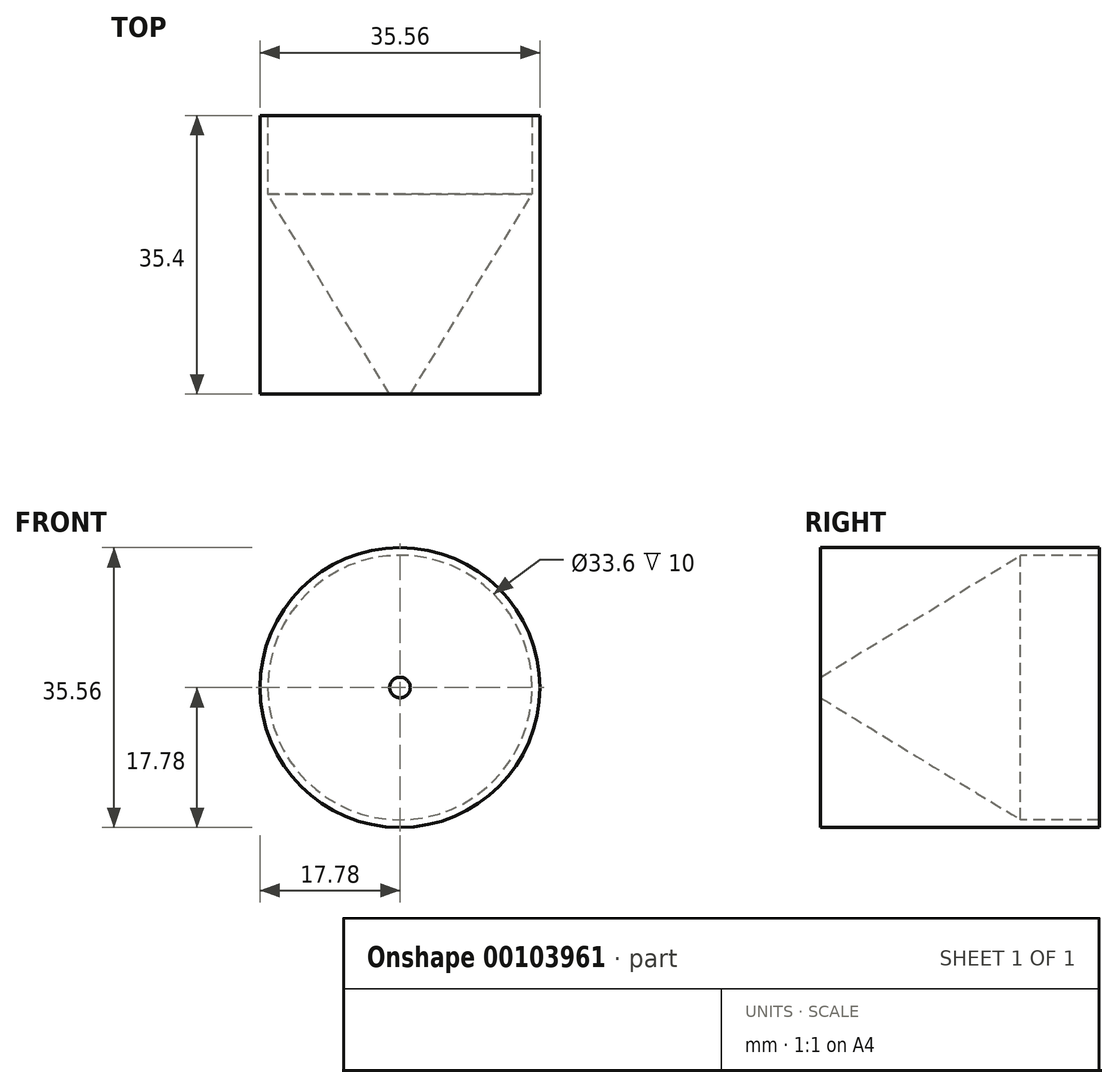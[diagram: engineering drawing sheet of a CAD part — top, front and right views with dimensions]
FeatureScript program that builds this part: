
annotation { "Feature Type Name" : "Feature", "Feature Type Description" : "" }
export const myFeature = defineFeature(function(context is Context, id is Id, definition is map)
    precondition{}
    {
        {
            var Q0;
            Q0=qCreatedBy(makeId("Front.planeOp"),FACE);
            var sketch = newSketch(context, id + "F0", { "sketchPlane" : qUnion([Q0])});
            skCircle(sketch, "E0", {"center": v(0, 0) * mm, "radius": 17.78 * mm});
            skSolve(sketch);
        }
        {
            var Q0;
            Q0 = qSketchRegion(id + "F0", true);
            extrude(context, id + "F1", {"entities" : qUnion([Q0]), "depth" : 25.4 * mm});
        }
        {
            var Q0;
            Q0=qCreatedBy(makeId("Top.planeOp"),FACE);
            var sketch = newSketch(context, id + "F2", { "sketchPlane" : qUnion([Q0])});
            skLineSegment(sketch, "E1", {"start": v(0, 0) * mm, "end": v(0, -25.4) * mm});
            skLineSegment(sketch, "E2", {"start": v(-16.8, 0) * mm, "end": v(0, 0) * mm});
            skLineSegment(sketch, "E3", {"start": v(0, -25.4) * mm, "end": v(-1.31, -25.4) * mm});
            skLineSegment(sketch, "E4", {"start": v(-1.31, -25.4) * mm, "end": v(-16.8, 0) * mm});
            skSolve(sketch);
        }
        {
            var Q0;
            Q0 = qSketchRegion(id + "F2", true);
            var Q1;
            Q1=sQuery(id+"F2.wireOp",EDGE,"E1");
            revolve(context, id + "F3", {"operationType" : NewBodyOperationType.REMOVE, "entities" : qUnion([Q0]), "axis" : qUnion([Q1]), "revolveType" : RevolveType.FULL, "oppositeDirection" : true});
        }
        {
            var Q0;
            Q0=makeQuery(id+"F1.opExtrude","CAP_FACE",FACE,{"disambiguationData":[OSD([sQuery(id+"F0.wireOp",EDGE,"E0")])],"isStart":true});
            var sketch = newSketch(context, id + "F4", { "sketchPlane" : qUnion([Q0])});
            skCircle(sketch, "E5", {"center": v(0, 0) * mm, "radius": 16.8 * mm});
            skCircle(sketch, "E6", {"center": v(0, 0) * mm, "radius": 17.78 * mm});
            skSolve(sketch);
        }
        {
            var Q0;
            Q0 = qSketchRegion(id + "F4", true);
            extrude(context, id + "F5", {"entities" : qUnion([Q0]), "operationType" : NewBodyOperationType.ADD, "depth" : 10 * mm});
        }
    });
